FCSTD DOCUMENT  (FreeCAD 1.0RUnknown)
Label: flip-stop
License: All rights reserved
LicenseURL: https://en.wikipedia.org/wiki/All_rights_reserved
objects: Image::ImagePlane×1, Sketcher::SketchObject×1, PartDesign::Body×1
note: 3 computed .brp shape members not serialized (recipe doc carries the construction recipe); baked Part::Feature solids carry a one-line shape summary decoded from their .brp

FEATURE [Image::ImagePlane] flip_stop_carabiner  label="flip-stop-carabiner"
  Placement = pos=(25.7644,8.21248,0) rot=(0,0,1;0.253073rad)
  XSize = 196.678
  YSize = 262.187
FEATURE [Sketcher::SketchObject] Sketch
  ArcFitTolerance = 1e-06
  AttachmentSupport = -> [XY_Plane]
  FullyConstrained = true
  MakeInternals = false
  MapMode = 5
  sketch-geometry (54):
    g0: ArcOfEllipse CenterX=0 CenterY=62.4 CenterZ=0 NormalX=0 NormalY=0 NormalZ=1 MajorRadius=5.35 MinorRadius=4.45 AngleXU=-1.5708 StartAngle=5.03728 EndAngle=7.52909
    g1: LineSegment [constr] StartX=0 StartY=57.05 StartZ=0 EndX=0 EndY=67.75 EndZ=0
    g2: LineSegment [constr] StartX=4.45 StartY=62.4 StartZ=0 EndX=-4.45 EndY=62.4 EndZ=0
    g3: GeomPoint [constr] X=0 Y=65.3698 Z=0
    g4: ArcOfEllipse CenterX=0 CenterY=37.9 CenterZ=0 NormalX=0 NormalY=0 NormalZ=1 MajorRadius=5.35 MinorRadius=4.45 AngleXU=-1.5708 StartAngle=5.03728 EndAngle=7.52909
    g5: LineSegment [constr] StartX=0 StartY=32.55 StartZ=0 EndX=0 EndY=43.25 EndZ=0
    g6: LineSegment [constr] StartX=4.45 StartY=37.9 StartZ=0 EndX=-4.45 EndY=37.9 EndZ=0
    g7: GeomPoint [constr] X=0 Y=34.9302 Z=0
    g8: GeomPoint [constr] X=0 Y=40.8698 Z=0
    g9: ArcOfEllipse CenterX=0 CenterY=7.6 CenterZ=0 NormalX=0 NormalY=0 NormalZ=1 MajorRadius=5.35 MinorRadius=4.45 AngleXU=-1.5708 StartAngle=5.03728 EndAngle=7.52909
    g10: LineSegment [constr] StartX=0 StartY=2.25 StartZ=0 EndX=0 EndY=12.95 EndZ=0
    g11: LineSegment [constr] StartX=4.45 StartY=7.6 StartZ=0 EndX=-4.45 EndY=7.6 EndZ=0
    g12: GeomPoint [constr] X=0 Y=4.63015 Z=0
    g13: GeomPoint [constr] X=0 Y=10.5698 Z=0
    g14: Ellipse CenterX=0 CenterY=7.6 CenterZ=0 NormalX=0 NormalY=0 NormalZ=1 MajorRadius=7.6 MinorRadius=6.7 AngleXU=-1.5708
    g15: LineSegment [constr] StartX=3e-16 StartY=0 StartZ=0 EndX=-3e-16 EndY=15.2 EndZ=0
    g16: LineSegment [constr] StartX=6.7 StartY=7.6 StartZ=0 EndX=-6.7 EndY=7.6 EndZ=0
    g17: GeomPoint [constr] X=1e-16 Y=4.01252 Z=0
    g18: GeomPoint [constr] X=-1e-16 Y=11.1875 Z=0
    g19: LineSegment [constr] StartX=-4.45 StartY=7.6 StartZ=0 EndX=-6.7 EndY=7.6 EndZ=0
    g20: LineSegment [constr] StartX=0 StartY=2.25 StartZ=0 EndX=0 EndY=0 EndZ=0
    g21: Ellipse CenterX=0 CenterY=37.9 CenterZ=0 NormalX=0 NormalY=0 NormalZ=1 MajorRadius=7.6 MinorRadius=6.7 AngleXU=-1.5708
    g22: LineSegment [constr] StartX=0 StartY=30.3 StartZ=0 EndX=9e-16 EndY=45.5 EndZ=0
    g23: LineSegment [constr] StartX=6.7 StartY=37.9 StartZ=0 EndX=-6.7 EndY=37.9 EndZ=0
    g24: GeomPoint [constr] X=0 Y=34.3125 Z=0
    g25: GeomPoint [constr] X=0 Y=41.4875 Z=0
    g26: Ellipse CenterX=0 CenterY=62.4 CenterZ=0 NormalX=0 NormalY=0 NormalZ=1 MajorRadius=7.6 MinorRadius=6.7 AngleXU=-1.5708
    g27: LineSegment [constr] StartX=2.7e-15 StartY=54.8 StartZ=0 EndX=0 EndY=70 EndZ=0
    g28: LineSegment [constr] StartX=6.7 StartY=62.4 StartZ=0 EndX=-6.7 EndY=62.4 EndZ=0
    g29: GeomPoint [constr] X=0 Y=58.8125 Z=0
    g30: GeomPoint [constr] X=0 Y=65.9875 Z=0
    g31: ArcOfCircle CenterX=-9.85 CenterY=19.5336 CenterZ=0 NormalX=0 NormalY=0 NormalZ=1 AngleXU=0 Radius=8.25 StartAngle=5.46007 EndAngle=6.28319
    g32: ArcOfCircle CenterX=-9.85 CenterY=25.9664 CenterZ=0 NormalX=0 NormalY=0 NormalZ=1 AngleXU=0 Radius=8.25 StartAngle=0 EndAngle=0.823113
    g33: LineSegment StartX=-1.6 StartY=25.9664 StartZ=0 EndX=-1.6 EndY=19.5336 EndZ=0
    g34: ArcOfCircle CenterX=9.85 CenterY=25.9664 CenterZ=0 NormalX=0 NormalY=0 NormalZ=1 AngleXU=0 Radius=8.25 StartAngle=2.31848 EndAngle=3.14159
    g35: ArcOfCircle CenterX=9.85 CenterY=19.5336 CenterZ=0 NormalX=0 NormalY=0 NormalZ=1 AngleXU=0 Radius=8.25 StartAngle=3.14159 EndAngle=3.96471
    g36: LineSegment StartX=1.6 StartY=25.9664 StartZ=0 EndX=1.6 EndY=19.5336 EndZ=0
    g37: ArcOfCircle CenterX=7.02232 CenterY=50.15 CenterZ=0 NormalX=0 NormalY=0 NormalZ=1 AngleXU=0 Radius=8.42232 StartAngle=2.55671 EndAngle=3.72648
    g38: ArcOfCircle CenterX=-7.02232 CenterY=50.15 CenterZ=0 NormalX=0 NormalY=0 NormalZ=1 AngleXU=0 Radius=8.42232 StartAngle=5.6983 EndAngle=6.86807
    g39: ArcOfCircle CenterX=-11.75 CenterY=52.5882 CenterZ=0 NormalX=0 NormalY=0 NormalZ=1 AngleXU=0 Radius=8.25 StartAngle=1e-16 EndAngle=0.638506
    g40: ArcOfCircle CenterX=-11.75 CenterY=47.7118 CenterZ=0 NormalX=0 NormalY=0 NormalZ=1 AngleXU=0 Radius=8.25 StartAngle=5.64468 EndAngle=6.28319
    g41: LineSegment StartX=-3.5 StartY=52.5882 StartZ=0 EndX=-3.5 EndY=47.7118 EndZ=0
    g42: ArcOfCircle CenterX=11.75 CenterY=52.5882 CenterZ=0 NormalX=0 NormalY=0 NormalZ=1 AngleXU=0 Radius=8.25 StartAngle=2.50309 EndAngle=3.14159
    g43: ArcOfCircle CenterX=11.75 CenterY=47.7118 CenterZ=0 NormalX=0 NormalY=0 NormalZ=1 AngleXU=0 Radius=8.25 StartAngle=3.14159 EndAngle=3.7801
    g44: LineSegment StartX=3.5 StartY=52.5882 StartZ=0 EndX=3.5 EndY=47.7118 EndZ=0
    g45: ArcOfCircle CenterX=5.05 CenterY=62.4 CenterZ=0 NormalX=0 NormalY=0 NormalZ=1 AngleXU=0 Radius=1.9 StartAngle=2.02452 EndAngle=4.25866
    g46: ArcOfCircle CenterX=-5.05 CenterY=7.6 CenterZ=0 NormalX=0 NormalY=0 NormalZ=1 AngleXU=0 Radius=1.9 StartAngle=5.16611 EndAngle=7.40026
    g47: ArcOfCircle CenterX=5.05 CenterY=7.6 CenterZ=0 NormalX=0 NormalY=0 NormalZ=1 AngleXU=0 Radius=1.9 StartAngle=2.02452 EndAngle=4.25866
    g48: ArcOfCircle CenterX=5.05 CenterY=37.9 CenterZ=0 NormalX=0 NormalY=0 NormalZ=1 AngleXU=0 Radius=1.9 StartAngle=2.02452 EndAngle=4.25866
    g49: ArcOfCircle CenterX=-5.05 CenterY=37.9 CenterZ=0 NormalX=0 NormalY=0 NormalZ=1 AngleXU=0 Radius=1.9 StartAngle=5.16611 EndAngle=7.40026
    g50: ArcOfCircle CenterX=-5.05 CenterY=62.4 CenterZ=0 NormalX=0 NormalY=0 NormalZ=1 AngleXU=0 Radius=1.9 StartAngle=5.16611 EndAngle=7.40026
    g51: ArcOfEllipse CenterX=0 CenterY=7.6 CenterZ=0 NormalX=0 NormalY=0 NormalZ=1 MajorRadius=5.35 MinorRadius=4.45 AngleXU=-1.5708 StartAngle=1.89569 EndAngle=4.3875
    g52: ArcOfEllipse CenterX=0 CenterY=37.9 CenterZ=0 NormalX=0 NormalY=0 NormalZ=1 MajorRadius=5.35 MinorRadius=4.45 AngleXU=-1.5708 StartAngle=1.89569 EndAngle=4.3875
    g53: ArcOfEllipse CenterX=0 CenterY=62.4 CenterZ=0 NormalX=0 NormalY=0 NormalZ=1 MajorRadius=5.35 MinorRadius=4.45 AngleXU=-1.5708 StartAngle=1.89569 EndAngle=4.3875
  constraints (118):
    c: InternalAlignment(g1,g0)
    c: InternalAlignment(g2,g0)
    c: InternalAlignment(g3,g0)
    c: InternalAlignment(g5-g8 -> g4) x4
    c: InternalAlignment(g10-g13 -> g9) x4
    c: Distance(g11,g11) = 8.9
    c: DistanceY(g10,g10) = 10.7
    c: Equal(g0,g9)
    c: PointOnObject(g4,g-2)
    c: PointOnObject(g9,g-2)
    c: Equal(g9,g4)
    c: PointOnObject(g13,g-2)
    c: PointOnObject(g8,g-2)
    c: PointOnObject(g3,g-2)
    c: InternalAlignment(g15-g18 -> g14) x4
    c: PointOnObject(g-1,g14)
    c: Coincident(g14,g9)
    c: Coincident(g19,g11)
    c: Coincident(g19,g16)
    c: Horizontal(g19)
    c: Distance(g19,g19) = 2.25
    c: Coincident(g20,g10)
    c: Coincident(g20,g-1)
    c: Equal(g20,g19)
    c: InternalAlignment(g22-g25 -> g21) x4
    c: Equal(g21,g14)
    c: Coincident(g21,g4)
    c: PointOnObject(g22,g-2)
    c: InternalAlignment(g27-g30 -> g26) x4
    c: Equal(g14,g26)
    c: PointOnObject(g27,g-2)
    c: PointOnObject(g0,g-2)
    c: Coincident(g26,g0)
    c: Vertical(g33)
    c: Equal(g32,g31)
    c: PointOnObject(g34,g21)
    c: PointOnObject(g35,g14)
    c: Tangent(g33,g31) = 1.5708
    c: Tangent(g33,g32) = 1.5708
    c: Coincident(g36,g34)
    c: Equal(g32,g34)
    c: Equal(g31,g35)
    c: Equal(g33,g36)
    c: Tangent(g34,g36,g34) = -1.5708
    c: Tangent(g36,g35) = -1.5708
    c: Vertical(g36)
    c: Horizontal(g33,g34)
    c: Horizontal(g31,g35)
    c: Radius(g31) = 8.25
    c: Tangent(g31,g14) = 1.5708
    c: Tangent(g32,g21) = 1.5708
    c: Coincident(g37,g27)
    c: Coincident(g37,g22)
    c: Coincident(g38,g27)
    c: Coincident(g38,g22)
    c: Equal(g37,g38)
    c: DistanceY(g22,g27) = 9.3
    c: Vertical(g41)
    c: Tangent(g39,g26) = 1.5708
    c: Tangent(g40,g21) = 1.5708
    c: Tangent(g41,g39) = 1.5708
    c: Equal(g39,g40)
    c: Tangent(g41,g40) = 1.5708
    c: Equal(g40,g31)
    c: Distance(g37,g41) = 2.1
    c: DistanceY(g20,g27) = 70  'total length'
    c: Vertical(g44)
    c: Equal(g42,g39)
    c: Tangent(g42,g26) = 1.5708
    c: Tangent(g43,g21) = 1.5708
    c: Tangent(g44,g42) = -1.5708
    c: Tangent(g44,g43) = -1.5708
    c: Symmetric(g43,g40,g-2)
    c: Distance(g-2,g41) = 3.5
    c: DistanceY(g15,g22) = 15.1
    c: Distance(g34,g32) = 3.2
    c: PointOnObject(g45,g53)
    c: PointOnObject(g45,g28)
    c: Radius(g46) = 1.9
    c: Symmetric(g46,g46,g11)
    c: Distance(g11,g46) = 1.3
    c: PointOnObject(g48,g52)
    c: Equal(g46,g47)
    c: PointOnObject(g47,g16)
    c: PointOnObject(g48,g23)
    c: PointOnObject(g49,g23)
    c: Equal(g49,g46)
    c: Equal(g48,g49)
    c: Vertical(g46,g49)
    c: Vertical(g50,g46)
    c: Equal(g50,g46)
    c: PointOnObject(g50,g28)
    c: Equal(g50,g45)
    c: Horizontal(g45,g50)
    c: Horizontal(g47,g46)
    c: PointOnObject(g47,g51)
    c: Horizontal(g49,g48)
    c: Coincident(g51,g46)
    c: PointOnObject(g9,g46)
    c: Equal(g9,g51)
    c: PointOnObject(g51,g47)
    c: Coincident(g9,g51)
    c: Coincident(g9,g47)
    c: Vertical(g47,g9)
    c: Coincident(g52,g49)
    c: Coincident(g4,g49)
    c: Equal(g4,g52)
    c: PointOnObject(g52,g48)
    c: Coincident(g4,g52)
    c: Coincident(g4,g48)
    c: Vertical(g48,g4)
    c: Coincident(g53,g50)
    c: Coincident(g0,g50)
    c: Equal(g0,g53)
    c: PointOnObject(g53,g45)
    c: Coincident(g0,g53)
    c: Coincident(g0,g45)
    c: Vertical(g45,g0)
FEATURE [PartDesign::Body] Body
  AllowCompound = false
  Group = -> [Sketch]
  Origin = -> Origin
